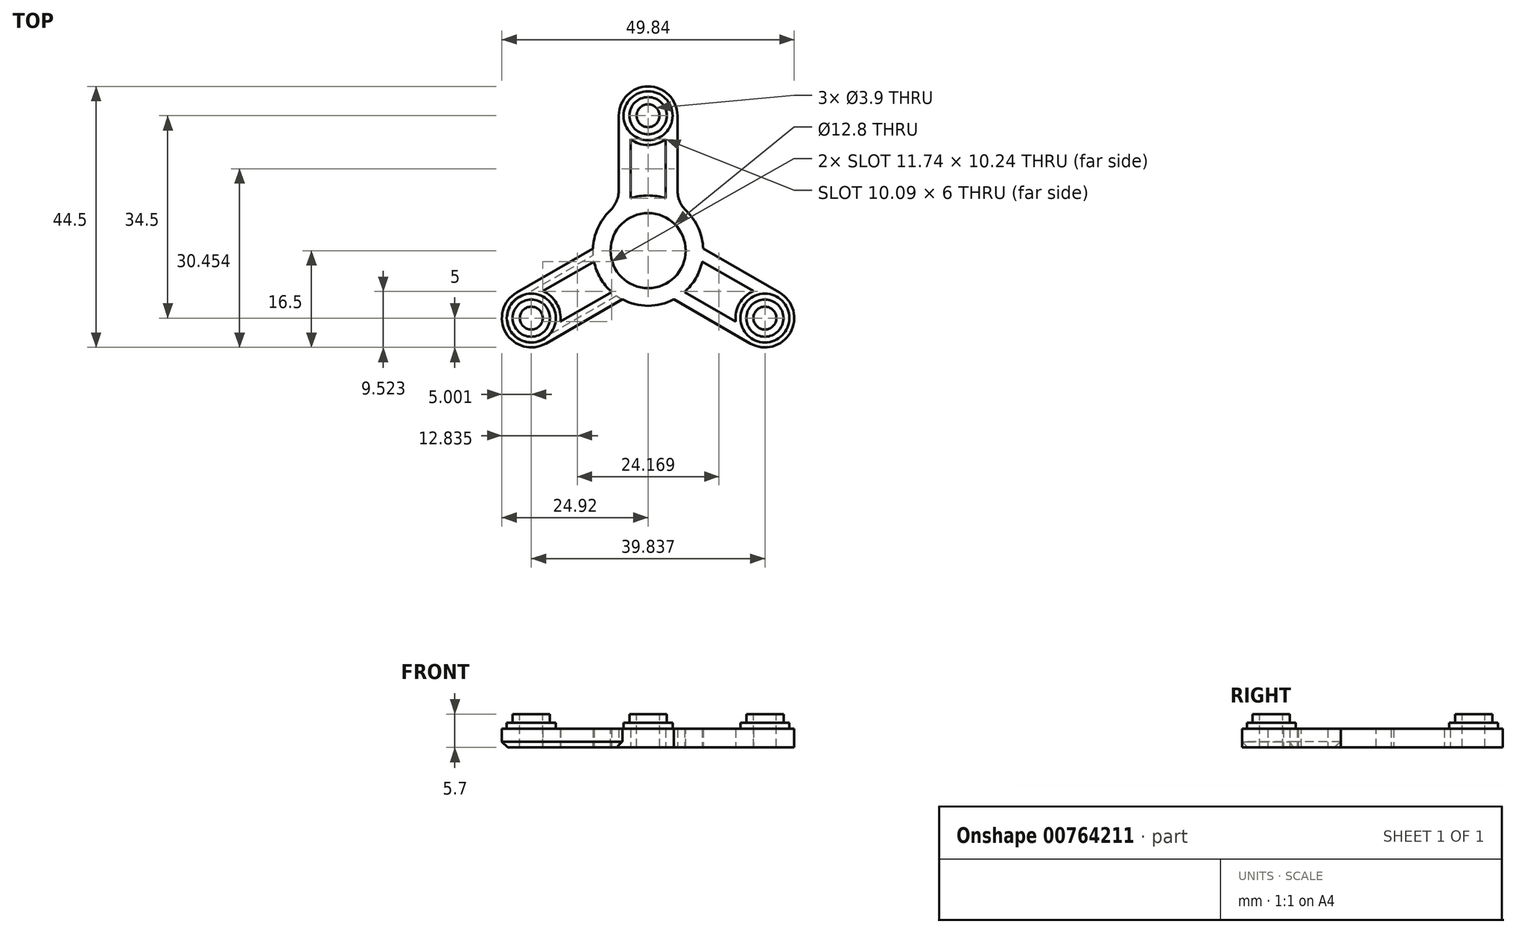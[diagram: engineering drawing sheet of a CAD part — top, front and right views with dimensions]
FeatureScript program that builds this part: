
annotation { "Feature Type Name" : "Feature", "Feature Type Description" : "" }
export const myFeature = defineFeature(function(context is Context, id is Id, definition is map)
    precondition{}
    {
        {
            var Q0;
            Q0=qCreatedBy(makeId("Top.planeOp"),FACE);
            var sketch = newSketch(context, id + "F0", { "sketchPlane" : qUnion([Q0])});
            skCircle(sketch, "E0", {"center": v(0, 0) * mm, "radius": 1.95 * mm, "construction": true});
            skCircle(sketch, "E1", {"center": v(0, 23) * mm, "radius": 1.95 * mm, "construction": true});
            skCircle(sketch, "E2.1.0", {"center": v(-19.92, -11.5) * mm, "radius": 1.95 * mm, "construction": true});
            skCircle(sketch, "E2.2.0", {"center": v(19.92, -11.5) * mm, "radius": 1.95 * mm, "construction": true});
            skLineSegment(sketch, "E3", {"start": v(0, 0) * mm, "end": v(32.17, 18.58) * mm, "construction": true});
            skLineSegment(sketch, "E4", {"start": v(0, 0) * mm, "end": v(-30.82, 17.8) * mm, "construction": true});
            skArc(sketch, "E5", {"start": v(-3, 19) * mm, "mid": v(0, 18) * mm, "end": v(3, 19) * mm});
            skCircle(sketch, "E6", {"center": v(0, 23) * mm, "radius": 11 * mm, "construction": true});
            skLineSegment(sketch, "E7", {"start": v(-7.1, 23) * mm, "end": v(7.08, 23) * mm, "construction": true});
            skLineSegment(sketch, "E8", {"start": v(-5, 23) * mm, "end": v(-5, 2.89) * mm});
            skLineSegment(sketch, "E9", {"start": v(5, 23) * mm, "end": v(5, 2.89) * mm});
            skLineSegment(sketch, "E10", {"start": v(-3, 19) * mm, "end": v(-3, 7.5) * mm});
            skLineSegment(sketch, "E11", {"start": v(3, 19) * mm, "end": v(3, 7.5) * mm});
            skArc(sketch, "E12.trimOffspring", {"start": v(5, 23) * mm, "mid": v(0, 28) * mm, "end": v(-5, 23) * mm});
            skLineSegment(sketch, "E13.1.0", {"start": v(-22.42, -7.17) * mm, "end": v(-5, 2.89) * mm, "construction": true});
            skLineSegment(sketch, "E13.1.1", {"start": v(-17.42, -15.83) * mm, "end": v(0, -5.77) * mm, "construction": true});
            skLineSegment(sketch, "E13.2.0", {"start": v(17.42, -15.83) * mm, "end": v(0, -5.77) * mm, "construction": true});
            skLineSegment(sketch, "E13.2.1", {"start": v(22.42, -7.17) * mm, "end": v(5, 2.89) * mm, "construction": true});
            skLineSegment(sketch, "E14", {"start": v(0, 5.77) * mm, "end": v(3, 7.5) * mm});
            skLineSegment(sketch, "E15.1.0", {"start": v(-14.95, -12.1) * mm, "end": v(-1.96, -4.6) * mm, "construction": true});
            skLineSegment(sketch, "E15.1.1", {"start": v(-17.95, -6.9) * mm, "end": v(-4.96, 0.6) * mm, "construction": true});
            skLineSegment(sketch, "E15.2.0", {"start": v(17.95, -6.9) * mm, "end": v(4.96, 0.6) * mm, "construction": true});
            skLineSegment(sketch, "E15.2.1", {"start": v(14.95, -12.1) * mm, "end": v(1.96, -4.6) * mm, "construction": true});
            skLineSegment(sketch, "E16.trimOffspring", {"start": v(0, 5.77) * mm, "end": v(-3, 7.5) * mm});
            skLineSegment(sketch, "E17", {"start": v(-5, 2.89) * mm, "end": v(0, 0) * mm});
            skLineSegment(sketch, "E18", {"start": v(0, 0) * mm, "end": v(5, 2.89) * mm});
            skCircle(sketch, "E19", {"center": v(0, 0) * mm, "radius": 6.4 * mm, "construction": true});
            skCircle(sketch, "E20.0", {"center": v(0, 0) * mm, "radius": 9.4 * mm});
            skSolve(sketch);
        }
        {
            var Q0;
            Q0 = qSketchRegion(id + "F0", true);
            extrude(context, id + "F1", {"entities" : qUnion([Q0]), "depth" : 3.2 * mm, "offsetDistance" : 25 * mm});
        }
        {
            var Q0;
            Q0=qCreatedBy(makeId("Right.planeOp"),FACE);
            var sketch = newSketch(context, id + "F2", { "sketchPlane" : qUnion([Q0])});
            skLineSegment(sketch, "E21", {"start": v(0, 0) * mm, "end": v(0, 39.16) * mm});
            skSolve(sketch);
        }
        {
            var Q0;
            Q0=makeQuery(id+"F1.opExtrude","SWEPT_BODY",BODY,{"disambiguationData":[OSD([sQuery(id+"F0.wireOp",EDGE,"E5"),sQuery(id+"F0.wireOp",EDGE,"E8"),sQuery(id+"F0.wireOp",EDGE,"E9"),sQuery(id+"F0.wireOp",EDGE,"E10"),sQuery(id+"F0.wireOp",EDGE,"E11"),sQuery(id+"F0.wireOp",EDGE,"E12.trimOffspring"),sQuery(id+"F0.wireOp",EDGE,"18b84ef0-d279-42b3-b95a-1ddac6aa847b.trimOffspring"),sQuery(id+"F0.wireOp",EDGE,"E14"),sQuery(id+"F0.wireOp",EDGE,"5123080d-cc78-4a68-8e78-a045bc30926f.trimOffspring"),sQuery(id+"F0.wireOp",EDGE,"ed31ea99-476c-43cf-ad8f-80f01553cb35.trimOffspring"),sQuery(id+"F0.wireOp",EDGE,"E16.trimOffspring"),sQuery(id+"F0.wireOp",EDGE,"e9033f68-9491-43eb-98a0-e927c0d29554.trimOffspring"),sQuery(id+"F0.wireOp",EDGE,"E17"),sQuery(id+"F0.wireOp",EDGE,"E18"),sQuery(id+"F0.wireOp",EDGE,"ccc4e442-ecce-4721-a327-a0c84df7cbbd.trimOffspring"),sQuery(id+"F0.wireOp",EDGE,"5347c399-d6ff-4045-8d49-987c9eddb6af.trimOffspring")])]});
            var Q1;
            Q1=sQuery(id+"F2.wireOp",EDGE,"E21");
            circularPattern(context, id + "F3", {"operationType" : NewBodyOperationType.ADD, "entities" : qUnion([Q0]), "axis" : qUnion([Q1]), "angle" : 360 * degree, "instanceCount" : 3, "equalSpace" : true});
        }
        {
            var Q0;
            {var subQ0=makeQuery(id+"F1.opExtrude","CAP_FACE",FACE,{"disambiguationData":[OSD([sQuery(id+"F0.wireOp",EDGE,"E5"),sQuery(id+"F0.wireOp",EDGE,"E8"),sQuery(id+"F0.wireOp",EDGE,"E9"),sQuery(id+"F0.wireOp",EDGE,"E10"),sQuery(id+"F0.wireOp",EDGE,"E11"),sQuery(id+"F0.wireOp",EDGE,"E12.trimOffspring"),sQuery(id+"F0.wireOp",EDGE,"18b84ef0-d279-42b3-b95a-1ddac6aa847b.trimOffspring"),sQuery(id+"F0.wireOp",EDGE,"E14"),sQuery(id+"F0.wireOp",EDGE,"5123080d-cc78-4a68-8e78-a045bc30926f.trimOffspring"),sQuery(id+"F0.wireOp",EDGE,"ed31ea99-476c-43cf-ad8f-80f01553cb35.trimOffspring"),sQuery(id+"F0.wireOp",EDGE,"E16.trimOffspring"),sQuery(id+"F0.wireOp",EDGE,"e9033f68-9491-43eb-98a0-e927c0d29554.trimOffspring"),sQuery(id+"F0.wireOp",EDGE,"E17"),sQuery(id+"F0.wireOp",EDGE,"E18"),sQuery(id+"F0.wireOp",EDGE,"ccc4e442-ecce-4721-a327-a0c84df7cbbd.trimOffspring"),sQuery(id+"F0.wireOp",EDGE,"5347c399-d6ff-4045-8d49-987c9eddb6af.trimOffspring")])],"isStart":false});Q0=makeQuery(id+"F3.boolean.opBoolean","MERGE",FACE,{"derivedFrom":[subQ0,makeQuery(id+"F3.opPattern","COPY",FACE,{"derivedFrom":subQ0,"instanceName":"1"}),makeQuery(id+"F3.opPattern","COPY",FACE,{"derivedFrom":subQ0,"instanceName":"2"})]});}
            var sketch = newSketch(context, id + "F4", { "sketchPlane" : qUnion([Q0])});
            skPoint(sketch, "E22", {"position": v(0, 23) * mm});
            skPoint(sketch, "E23", {"position": v(-19.92, -11.5) * mm});
            skPoint(sketch, "E24", {"position": v(19.92, -11.5) * mm});
            skCircle(sketch, "E25", {"center": v(0, 23) * mm, "radius": 4.17 * mm});
            skCircle(sketch, "E26.1.0", {"center": v(-19.92, -11.5) * mm, "radius": 4.17 * mm});
            skCircle(sketch, "E26.2.0", {"center": v(19.92, -11.5) * mm, "radius": 4.17 * mm});
            skPoint(sketch, "E26.center", {"position": v(0, 0) * mm});
            skSolve(sketch);
        }
        {
            var Q0;
            Q0 = qSketchRegion(id + "F4", true);
            extrude(context, id + "F5", {"entities" : qUnion([Q0]), "operationType" : NewBodyOperationType.ADD, "depth" : 1 * mm, "offsetDistance" : 25 * mm});
        }
        {
            var Q0;
            Q0=makeQuery(id+"F5.opExtrude","CAP_FACE",FACE,{"disambiguationData":[OSD([sQuery(id+"F4.wireOp",EDGE,"E25")])],"isStart":false});
            var sketch = newSketch(context, id + "F6", { "sketchPlane" : qUnion([Q0])});
            skCircle(sketch, "E27", {"center": v(0, 23) * mm, "radius": 3.17 * mm});
            skCircle(sketch, "E28.1.0", {"center": v(-19.92, -11.5) * mm, "radius": 3.17 * mm});
            skCircle(sketch, "E28.2.0", {"center": v(19.92, -11.5) * mm, "radius": 3.17 * mm});
            skPoint(sketch, "E28.center", {"position": v(0, 0) * mm});
            skSolve(sketch);
        }
        {
            var Q0;
            Q0 = qSketchRegion(id + "F6", true);
            extrude(context, id + "F7", {"entities" : qUnion([Q0]), "operationType" : NewBodyOperationType.ADD, "depth" : 1.5 * mm, "offsetDistance" : 25 * mm});
        }
        {
            var Q0;
            Q0=makeQuery(id+"F7.opExtrude","CAP_FACE",FACE,{"disambiguationData":[OSD([sQuery(id+"F6.wireOp",EDGE,"E27")])],"isStart":false});
            var sketch = newSketch(context, id + "F8", { "sketchPlane" : qUnion([Q0])});
            skCircle(sketch, "E29", {"center": v(0, 23) * mm, "radius": 1.95 * mm});
            skCircle(sketch, "E30.1.0", {"center": v(-19.92, -11.5) * mm, "radius": 1.95 * mm});
            skCircle(sketch, "E30.2.0", {"center": v(19.92, -11.5) * mm, "radius": 1.95 * mm});
            skPoint(sketch, "E30.center", {"position": v(0, 0) * mm});
            skSolve(sketch);
        }
        {
            var Q0;
            Q0 = qSketchRegion(id + "F8", true);
            extrude(context, id + "F9", {"entities" : qUnion([Q0]), "operationType" : NewBodyOperationType.REMOVE, "endBound" : BoundingType.UP_TO_NEXT, "oppositeDirection" : true, "depth" : 25 * mm, "offsetDistance" : 25 * mm});
        }
        {
            var Q0;
            {var subQ0=makeQuery(id+"F1.opExtrude","CAP_FACE",FACE,{"disambiguationData":[OSD([sQuery(id+"F0.wireOp",EDGE,"E5"),sQuery(id+"F0.wireOp",EDGE,"E8"),sQuery(id+"F0.wireOp",EDGE,"E9"),sQuery(id+"F0.wireOp",EDGE,"E10"),sQuery(id+"F0.wireOp",EDGE,"E11"),sQuery(id+"F0.wireOp",EDGE,"E12.trimOffspring"),sQuery(id+"F0.wireOp",EDGE,"E14"),sQuery(id+"F0.wireOp",EDGE,"E16.trimOffspring"),sQuery(id+"F0.wireOp",EDGE,"E20.0")])],"isStart":false});Q0=makeQuery(id+"F3.boolean.opBoolean","MERGE",FACE,{"derivedFrom":[subQ0,makeQuery(id+"F3.opPattern","COPY",FACE,{"derivedFrom":subQ0,"instanceName":"1"}),makeQuery(id+"F3.opPattern","COPY",FACE,{"derivedFrom":subQ0,"instanceName":"2"})]});}
            var sketch = newSketch(context, id + "F10", { "sketchPlane" : qUnion([Q0])});
            skCircle(sketch, "E31", {"center": v(0, 0) * mm, "radius": 6.4 * mm});
            skSolve(sketch);
        }
        {
            var Q0;
            Q0 = qSketchRegion(id + "F10", true);
            extrude(context, id + "F11", {"entities" : qUnion([Q0]), "operationType" : NewBodyOperationType.REMOVE, "oppositeDirection" : true, "depth" : 25 * mm, "offsetDistance" : 25 * mm});
        }
        {
            var Q0;
            Q0=makeQuery(id+"F1.opExtrude","SWEPT_EDGE",EDGE,{"disambiguationData":[OSD([sQuery(id+"F0.wireOp",EDGE,"E8"),sQuery(id+"F0.wireOp",EDGE,"E20.0")])]});
            var Q1;
            Q1=makeQuery(id+"F3.opPattern","COPY",EDGE,{"derivedFrom":makeQuery(id+"F1.opExtrude","SWEPT_EDGE",EDGE,{"disambiguationData":[OSD([sQuery(id+"F0.wireOp",EDGE,"E9"),sQuery(id+"F0.wireOp",EDGE,"E20.0")])]}),"instanceName":"1"});
            var Q2;
            Q2=makeQuery(id+"F3.opPattern","COPY",EDGE,{"derivedFrom":makeQuery(id+"F1.opExtrude","SWEPT_EDGE",EDGE,{"disambiguationData":[OSD([sQuery(id+"F0.wireOp",EDGE,"E8"),sQuery(id+"F0.wireOp",EDGE,"E20.0")])]}),"instanceName":"1"});
            var Q3;
            Q3=makeQuery(id+"F3.opPattern","COPY",EDGE,{"derivedFrom":makeQuery(id+"F1.opExtrude","SWEPT_EDGE",EDGE,{"disambiguationData":[OSD([sQuery(id+"F0.wireOp",EDGE,"E9"),sQuery(id+"F0.wireOp",EDGE,"E20.0")])]}),"instanceName":"2"});
            var Q4;
            Q4=makeQuery(id+"F3.opPattern","COPY",EDGE,{"derivedFrom":makeQuery(id+"F1.opExtrude","SWEPT_EDGE",EDGE,{"disambiguationData":[OSD([sQuery(id+"F0.wireOp",EDGE,"E8"),sQuery(id+"F0.wireOp",EDGE,"E20.0")])]}),"instanceName":"2"});
            var Q5;
            Q5=makeQuery(id+"F1.opExtrude","SWEPT_EDGE",EDGE,{"disambiguationData":[OSD([sQuery(id+"F0.wireOp",EDGE,"E9"),sQuery(id+"F0.wireOp",EDGE,"E20.0")])]});
            fillet(context, id + "F12", {"entities" : qUnion([Q0, Q1, Q2, Q3, Q4, Q5]), "radius" : 5 * mm, "tangentPropagation" : true, "allowEdgeOverflow" : false});
        }
        {
            var Q0;
            Q0=makeQuery(id+"F3.opPattern","COPY",EDGE,{"derivedFrom":makeQuery(id+"F1.opExtrude","CAP_EDGE",EDGE,{"disambiguationData":[OSD([sQuery(id+"F0.wireOp",EDGE,"E12.trimOffspring")])],"isStart":true}),"instanceName":"1"});
            chamfer(context, id + "F13", {"entities" : qUnion([Q0]), "width" : 1 * mm, "tangentPropagation" : true});
        }
    });
